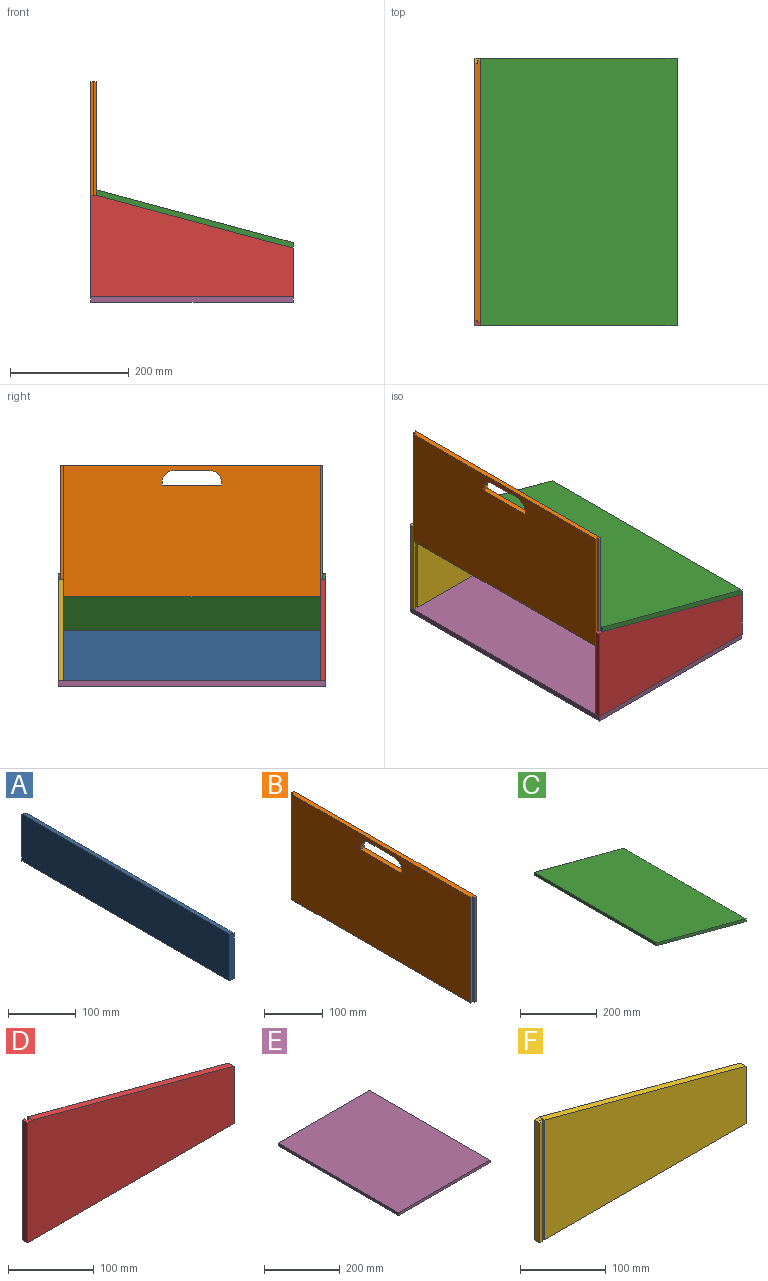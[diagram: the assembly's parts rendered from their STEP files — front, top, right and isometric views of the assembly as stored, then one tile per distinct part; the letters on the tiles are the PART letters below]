
ASSEMBLY  parts=6 mates=6
PART A: 6 faces, bbox 9x432x84.4 mm
  f0: plane 432x9mm, normal (0,0,-1), area 3888mm2, adj f1,f3,f4,f5
  f1: plane 432x84.4mm, normal (-1,0,0), area 36462mm2, adj f0,f2,f4,f5
  f2: plane 432x9mm, normal (0.26,0,0.97), area 4025.2mm2, adj f1,f3,f4,f5
  f3: plane 432x81.99mm, normal (1,0,0), area 35420.3mm2, adj f0,f2,f4,f5
  f4: plane 84.4x9mm, normal (0,1,0), area 748.8mm2, adj f0,f1,f2,f3
  f5: plane 84.4x9mm, normal (0,-1,0), area 748.8mm2, adj f0,f1,f2,f3
PART B: 16 faces, bbox 9x440.5x220.7 mm
  f0: plane 440.5x220.68mm, normal (1,0,0), area 94882.3mm2, adj f2,f5,f6,f9,f10,f11,f12,f13
  f1: plane 432x220.68mm, normal (-1,0,0), area 93006.5mm2, adj f2,f3,f8,f9,f10,f11,f12,f13
  f2: plane 440.5x9mm, normal (0,0,-1), area 3926.2mm2, adj f0,f1,f3,f4,f5,f6,f7,f8
  f3: plane 220.68x4.5mm, normal (0,-1,0), area 993.1mm2, adj f1,f2,f4,f9
  f4: plane 220.68x4mm, normal (-1,0,0), area 882.7mm2, adj f2,f3,f5,f9
  f5: plane 220.68x4.5mm, normal (0,-1,0), area 993.1mm2, adj f0,f2,f4,f9
  f6: plane 220.68x4.5mm, normal (0,1,0), area 993.1mm2, adj f0,f2,f7,f9
  f7: plane 220.68x4.5mm, normal (-1,0,0), area 993.1mm2, adj f2,f6,f8,f9
  f8: plane 220.68x4.5mm, normal (0,1,0), area 993.1mm2, adj f1,f2,f7,f9
  f9: plane 440.5x9mm, normal (0,0,1), area 3926.2mm2, adj f0,f1,f3,f4,f5,f6,f7,f8
  f10: plane 9x5mm, normal (0,1,0), area 45mm2, adj f0,f1,f12,f15
  f11: plane 60x9mm, normal (0,0,-1), area 540mm2, adj f0,f1,f14,f15
  f12: plane 100x9mm, normal (0,0,1), area 900mm2, adj f0,f1,f10,f13
  f13: plane 9x5mm, normal (0,-1,0), area 45mm2, adj f0,f1,f12,f14
  f14: cylinder r=20mm len=20mm, axis (1,0,0), area 282.7mm2, adj f0,f1,f11,f13
  f15: cylinder r=20mm len=20mm, axis (-1,0,0), area 282.7mm2, adj f0,f1,f10,f11
PART C: 6 faces, bbox 331x450x98 mm
  f0: plane 450x331mm, normal (-0.26,0,-0.97), area 154204.4mm2, adj f1,f3,f4,f5
  f1: plane 450x9.32mm, normal (-1,0,0), area 4192.9mm2, adj f0,f2,f4,f5
  f2: plane 450x331mm, normal (0.26,0,0.97), area 154204.4mm2, adj f1,f3,f4,f5
  f3: plane 450x9.32mm, normal (1,0,0), area 4192.9mm2, adj f0,f2,f4,f5
  f4: plane 331x98.01mm, normal (0,1,0), area 3084.1mm2, adj f0,f1,f2,f3
  f5: plane 331x98.01mm, normal (0,-1,0), area 3084.1mm2, adj f0,f1,f2,f3
PART D: 11 faces, bbox 340x9x170.7 mm
  f0: plane 331x170.68mm, normal (0,1,0), area 41817.5mm2, adj f4,f5,f7,f9
  f1: plane 9x9mm, normal (0,0,1), area 63mm2, adj f2,f3,f6,f7,f8,f10
  f2: plane 170.68x9mm, normal (-1,0,0), area 1536.1mm2, adj f1,f3,f4,f6
  f3: plane 340x170.68mm, normal (0,-1,0), area 43353.7mm2, adj f1,f2,f4,f5,f7
  f4: plane 340x9mm, normal (0,0,-1), area 3042mm2, adj f0,f2,f3,f5,f6,f8,f9,f10
  f5: plane 81.99x9mm, normal (1,0,0), area 737.9mm2, adj f0,f3,f4,f7
  f6: plane 170.68x4.5mm, normal (0,1,0), area 768.1mm2, adj f1,f2,f4,f8
  f7: plane 331x88.69mm, normal (0.26,0,0.97), area 3084.1mm2, adj f0,f1,f3,f5,f9
  f8: plane 170.68x4mm, normal (1,0,0), area 682.7mm2, adj f1,f4,f6,f10
  f9: plane 170.68x4mm, normal (-1,0,0), area 682.7mm2, adj f0,f4,f7,f10
  f10: plane 170.68x4.5mm, normal (0,1,0), area 768.1mm2, adj f1,f4,f8,f9
PART E: 6 faces, bbox 340x450x9 mm
  f0: plane 450x9mm, normal (-1,0,0), area 4050mm2, adj f1,f3,f4,f5
  f1: plane 340x9mm, normal (0,-1,0), area 3060mm2, adj f0,f2,f4,f5
  f2: plane 450x9mm, normal (1,0,0), area 4050mm2, adj f1,f3,f4,f5
  f3: plane 340x9mm, normal (0,1,0), area 3060mm2, adj f0,f2,f4,f5
  f4: plane 450x340mm, normal (0,0,1), area 153000mm2, adj f0,f1,f2,f3
  f5: plane 450x340mm, normal (0,0,-1), area 153000mm2, adj f0,f1,f2,f3
PART F: 11 faces, bbox 340x9x170.7 mm
  f0: plane 331x170.68mm, normal (0,-1,0), area 41817.5mm2, adj f4,f5,f7,f9
  f1: plane 9x9mm, normal (0,0,1), area 63mm2, adj f2,f3,f6,f7,f8,f10
  f2: plane 170.68x9mm, normal (-1,0,0), area 1536.1mm2, adj f1,f3,f4,f6
  f3: plane 340x170.68mm, normal (0,1,0), area 43353.7mm2, adj f1,f2,f4,f5,f7
  f4: plane 340x9mm, normal (0,0,-1), area 3042mm2, adj f0,f2,f3,f5,f6,f8,f9,f10
  f5: plane 81.99x9mm, normal (1,0,0), area 737.9mm2, adj f0,f3,f4,f7
  f6: plane 170.68x4.5mm, normal (0,-1,0), area 768.1mm2, adj f1,f2,f4,f8
  f7: plane 331x88.69mm, normal (0.26,0,0.97), area 3084.1mm2, adj f0,f1,f3,f5,f9
  f8: plane 170.68x4mm, normal (1,0,0), area 682.7mm2, adj f1,f4,f6,f10
  f9: plane 170.68x4mm, normal (-1,0,0), area 682.7mm2, adj f0,f4,f7,f10
  f10: plane 170.68x4.5mm, normal (0,-1,0), area 768.1mm2, adj f1,f4,f8,f9
PLACE A t=(-16.33,-64.16,96.16)mm
PLACE B t=(-16.33,-64.16,237.2)mm
PLACE C t=(-16.33,-73.16,96.16)mm
PLACE D t=(-16.33,-64.16,96.16)mm
PLACE E t=(-53.2,229.74,-23.82)mm
PLACE F t=(-16.33,385.84,96.16)mm
MATE fastened E.f4 <-> F.f4  axis (0,0,1) through (301.18,376.84,-14.82)mm
MATE planar B.f4 <-> D.f8  axis (-1,0,0) through (-34.32,-66.16,236.56)mm
MATE planar B.f5 <-> D.f10  axis (0,-1,0) through (-32.07,-68.16,236.56)mm
MATE fastened F.f0 <-> A.f4  axis (0,-1,0) through (301.18,367.84,67.17)mm
MATE fastened A.f5 <-> D.f0  axis (0,-1,0) through (301.18,-64.16,-14.82)mm
MATE fastened C.f5 <-> D.f3  axis (0,-1,0) through (301.18,-73.16,67.17)mm
